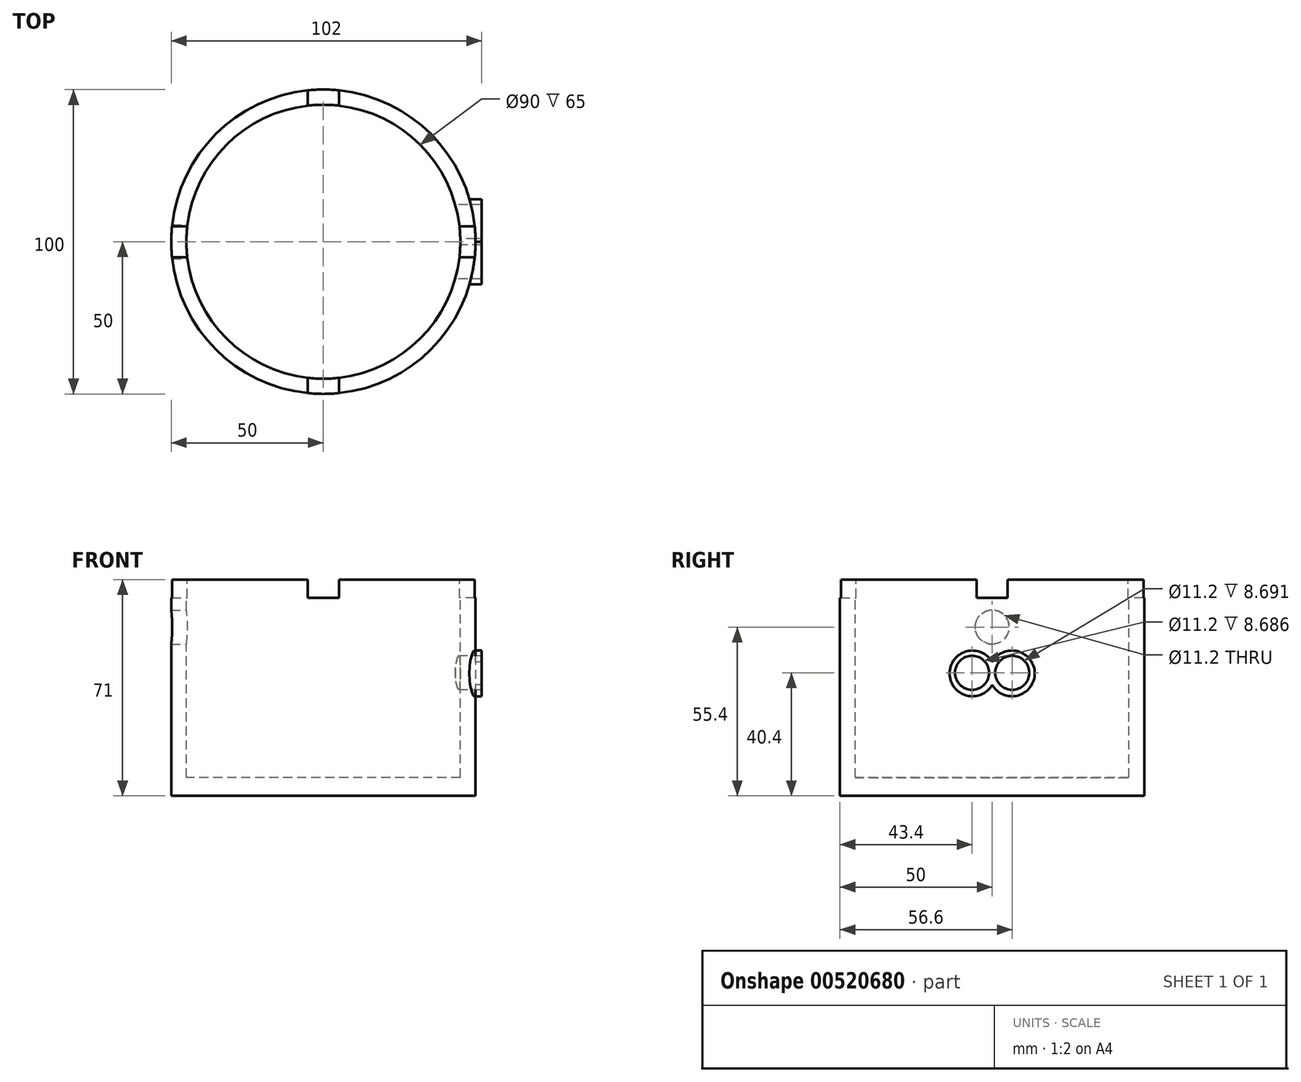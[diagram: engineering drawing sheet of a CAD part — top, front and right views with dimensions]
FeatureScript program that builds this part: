
annotation { "Feature Type Name" : "Feature", "Feature Type Description" : "" }
export const myFeature = defineFeature(function(context is Context, id is Id, definition is map)
    precondition{}
    {
        {
            var Q0;
            Q0=qCreatedBy(makeId("Top.planeOp"),FACE);
            var sketch = newSketch(context, id + "F0", { "sketchPlane" : qUnion([Q0])});
            skCircle(sketch, "E0", {"center": v(0, 0) * mm, "radius": 50 * mm});
            skSolve(sketch);
        }
        {
            var Q0;
            Q0=qSketchRegion(id+"F0",true);
            extrude(context, id + "F1", {"entities" : qUnion([Q0]), "depth" : 71 * mm, "offsetDistance" : 25 * mm});
        }
        {
            var Q0;
            Q0=makeQuery(id+"F1.opExtrude","CAP_FACE",FACE,{"disambiguationData":[OSD([sQuery(id+"F0.wireOp",EDGE,"E0")])],"isStart":false});
            var sketch = newSketch(context, id + "F2", { "sketchPlane" : qUnion([Q0])});
            skCircle(sketch, "E1", {"center": v(0, 0) * mm, "radius": 45 * mm});
            skSolve(sketch);
        }
        {
            var Q0;
            Q0=qSketchRegion(id+"F2",true);
            extrude(context, id + "F3", {"entities" : qUnion([Q0]), "operationType" : NewBodyOperationType.REMOVE, "oppositeDirection" : true, "depth" : 65 * mm, "offsetDistance" : 25 * mm});
        }
        {
            var Q0;
            Q0=qCreatedBy(makeId("Front.planeOp"),FACE);
            var sketch = newSketch(context, id + "F4", { "sketchPlane" : qUnion([Q0])});
            skLineSegment(sketch, "E2.bottom", {"start": v(5.1, 71) * mm, "end": v(-5.1, 71) * mm});
            skLineSegment(sketch, "E2.top", {"start": v(5.1, 65) * mm, "end": v(-5.1, 65) * mm});
            skLineSegment(sketch, "E2.left", {"start": v(5.1, 71) * mm, "end": v(5.1, 65) * mm});
            skLineSegment(sketch, "E2.right", {"start": v(-5.1, 71) * mm, "end": v(-5.1, 65) * mm});
            skSolve(sketch);
        }
        {
            var Q0;
            Q0=qSketchRegion(id+"F4",true);
            extrude(context, id + "F5", {"entities" : qUnion([Q0]), "operationType" : NewBodyOperationType.REMOVE, "oppositeDirection" : true, "depth" : 50 * mm, "offsetDistance" : 25 * mm});
        }
        {
            var Q0;
            Q0=qCreatedBy(makeId("Front.planeOp"),FACE);
            var sketch = newSketch(context, id + "F6", { "sketchPlane" : qUnion([Q0])});
            skLineSegment(sketch, "E3.bottom", {"start": v(5.1, 71) * mm, "end": v(-5.1, 71) * mm});
            skLineSegment(sketch, "E3.top", {"start": v(5.1, 65) * mm, "end": v(-5.1, 65) * mm});
            skLineSegment(sketch, "E3.left", {"start": v(5.1, 71) * mm, "end": v(5.1, 65) * mm});
            skLineSegment(sketch, "E3.right", {"start": v(-5.1, 71) * mm, "end": v(-5.1, 65) * mm});
            skSolve(sketch);
        }
        {
            var Q0;
            Q0=qSketchRegion(id+"F6",true);
            extrude(context, id + "F7", {"entities" : qUnion([Q0]), "operationType" : NewBodyOperationType.REMOVE, "depth" : 50 * mm, "offsetDistance" : 25 * mm});
        }
        {
            var Q0;
            Q0=qCreatedBy(makeId("Right.planeOp"),FACE);
            var sketch = newSketch(context, id + "F8", { "sketchPlane" : qUnion([Q0])});
            skLineSegment(sketch, "E4.bottom", {"start": v(5.1, 71) * mm, "end": v(-5.1, 71) * mm});
            skLineSegment(sketch, "E4.top", {"start": v(5.1, 65) * mm, "end": v(-5.1, 65) * mm});
            skLineSegment(sketch, "E4.left", {"start": v(5.1, 71) * mm, "end": v(5.1, 65) * mm});
            skLineSegment(sketch, "E4.right", {"start": v(-5.1, 71) * mm, "end": v(-5.1, 65) * mm});
            skSolve(sketch);
        }
        {
            var Q0;
            Q0=qSketchRegion(id+"F8",true);
            extrude(context, id + "F9", {"entities" : qUnion([Q0]), "operationType" : NewBodyOperationType.REMOVE, "oppositeDirection" : true, "depth" : 50 * mm, "offsetDistance" : 25 * mm});
        }
        {
            var Q0;
            Q0=qCreatedBy(makeId("Right.planeOp"),FACE);
            var sketch = newSketch(context, id + "F10", { "sketchPlane" : qUnion([Q0])});
            skLineSegment(sketch, "E5.bottom", {"start": v(5.1, 71) * mm, "end": v(-5.1, 71) * mm});
            skLineSegment(sketch, "E5.top", {"start": v(5.1, 65) * mm, "end": v(-5.1, 65) * mm});
            skLineSegment(sketch, "E5.left", {"start": v(5.1, 71) * mm, "end": v(5.1, 65) * mm});
            skLineSegment(sketch, "E5.right", {"start": v(-5.1, 71) * mm, "end": v(-5.1, 65) * mm});
            skSolve(sketch);
        }
        {
            var Q0;
            Q0=qSketchRegion(id+"F10",true);
            extrude(context, id + "F11", {"entities" : qUnion([Q0]), "operationType" : NewBodyOperationType.REMOVE, "depth" : 50 * mm, "offsetDistance" : 25 * mm});
        }
        {
            var Q0;
            Q0=qCreatedBy(makeId("Right.planeOp"),FACE);
            var sketch = newSketch(context, id + "F12", { "sketchPlane" : qUnion([Q0])});
            skCircle(sketch, "E6", {"center": v(0, 55.4) * mm, "radius": 5.6 * mm});
            skSolve(sketch);
        }
        {
            var Q0;
            Q0=qSketchRegion(id+"F12",true);
            extrude(context, id + "F13", {"entities" : qUnion([Q0]), "operationType" : NewBodyOperationType.REMOVE, "oppositeDirection" : true, "depth" : 55 * mm, "offsetDistance" : 25 * mm});
        }
        {
            var Q0;
            Q0=qCreatedBy(makeId("Right.planeOp"),FACE);
            var sketch = newSketch(context, id + "F14", { "sketchPlane" : qUnion([Q0])});
            skCircle(sketch, "E7", {"center": v(-6.6, 40.4) * mm, "radius": 5.6 * mm});
            skCircle(sketch, "E8", {"center": v(6.6, 40.4) * mm, "radius": 5.6 * mm});
            skSolve(sketch);
        }
        {
            var Q0;
            Q0=qSketchRegion(id+"F14",true);
            extrude(context, id + "F15", {"entities" : qUnion([Q0]), "operationType" : NewBodyOperationType.REMOVE, "depth" : 56 * mm, "offsetDistance" : 25 * mm});
        }
        {
            var Q0;
            Q0=qCreatedBy(makeId("Right.planeOp"),FACE);
            var sketch = newSketch(context, id + "F16", { "sketchPlane" : qUnion([Q0])});
            skCircle(sketch, "E9", {"center": v(-6.5, 40.18) * mm, "radius": 7.5 * mm});
            skCircle(sketch, "E10", {"center": v(6.5, 40.18) * mm, "radius": 7.5 * mm});
            skSolve(sketch);
        }
        {
            var Q0;
            Q0=qSketchRegion(id+"F16",true);
            extrude(context, id + "F17", {"entities" : qUnion([Q0]), "operationType" : NewBodyOperationType.ADD, "depth" : 52 * mm, "offsetDistance" : 25 * mm});
        }
        {
            var Q0;
            Q0=qSketchRegion(id+"F14",true);
            extrude(context, id + "F18", {"entities" : qUnion([Q0]), "operationType" : NewBodyOperationType.REMOVE, "depth" : 55 * mm, "offsetDistance" : 25 * mm});
        }
        {
            var Q0;
            Q0=makeQuery(id+"F3.boolean.opBoolean","COPY",FACE,{"derivedFrom":makeQuery(id+"F3.opExtrude","CAP_FACE",FACE,{"disambiguationData":[OSD([sQuery(id+"F2.wireOp",EDGE,"E1")])],"isStart":false})});
            var sketch = newSketch(context, id + "F19", { "sketchPlane" : qUnion([Q0])});
            skCircle(sketch, "E11", {"center": v(0, 0) * mm, "radius": 45 * mm});
            skSolve(sketch);
        }
        {
            var Q0;
            Q0=qSketchRegion(id+"F19",true);
            extrude(context, id + "F20", {"entities" : qUnion([Q0]), "operationType" : NewBodyOperationType.REMOVE, "depth" : 50 * mm, "offsetDistance" : 25 * mm});
        }
    });
